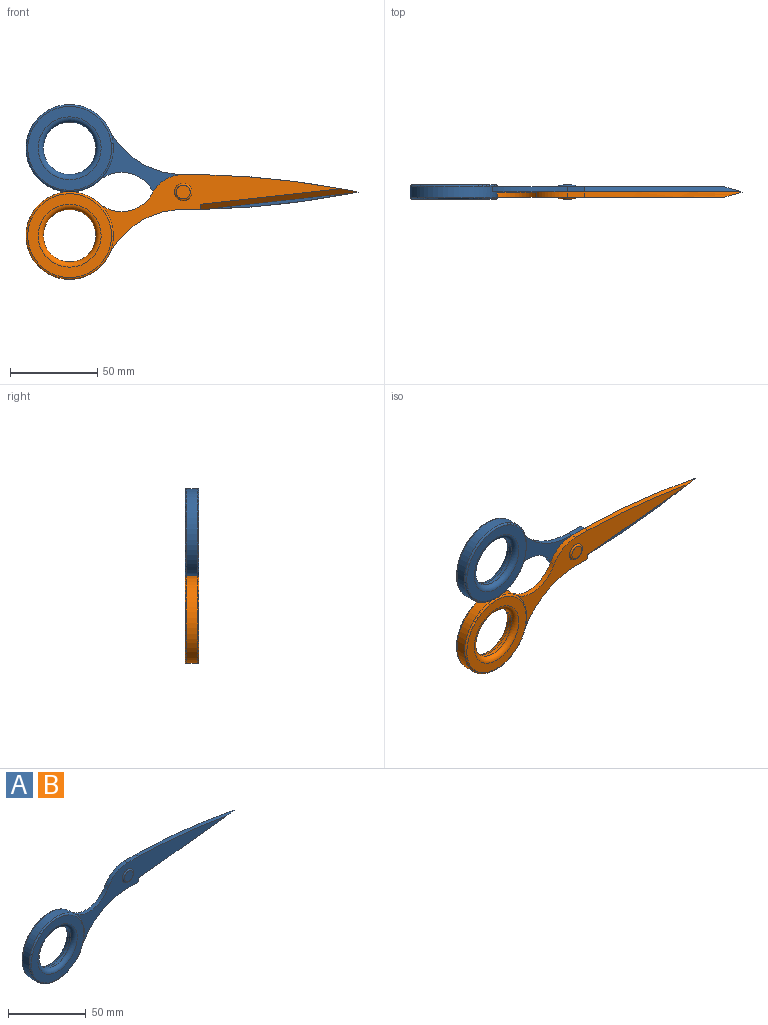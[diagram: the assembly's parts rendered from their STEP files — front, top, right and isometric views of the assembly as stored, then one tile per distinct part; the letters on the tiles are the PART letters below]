
ASSEMBLY  parts=2 mates=1
PART A: 20 faces, bbox 192.1x8x62.1 mm
  f0: plane 138.65x46.27mm, normal (0,-1,0), area 1502.5mm2, adj f2,f3,f4,f6,f7,f8,f13,f14
  f1: plane 148.49x46.27mm, normal (0,1,0), area 1836.4mm2, adj f2,f3,f4,f5,f6,f7,f8,f13
  f2: cylinder r=47.81mm len=42.68mm, axis (0,1,0), area 158.3mm2, adj f0,f1,f5,f6
  f3: cylinder r=20mm len=17.32mm, axis (0,1,0), area 62.8mm2, adj f0,f1,f4,f8
  f4: cylinder r=20mm len=31.17mm, axis (0,1,0), area 110.2mm2, adj f0,f1,f3,f5
  f5: cylinder r=25mm len=50mm, axis (0,1,0), area 843.7mm2, adj f1,f2,f4,f17,f18
  f6: plane 10x3mm, normal (0,0,-1), area 30mm2, adj f0,f1,f2,f14
  f7: cylinder r=500mm len=90mm, axis (0,1,0), area 257.2mm2, adj f0,f1,f8,f13
  f8: plane 10x3mm, normal (0,0,1), area 30mm2, adj f0,f1,f3,f7
  f9: plane 48x48mm, normal (0,1,0), area 791.7mm2, adj f16,f17
  f10: cylinder r=15mm len=30mm, axis (0,1,0), area 188.5mm2, adj f15,f16
  f11: plane 48x48mm, normal (0,-1,0), area 791.7mm2, adj f15,f18
  f12: plane 8x8mm, normal (0,-1,0), area 50.3mm2, adj f19
  f13: plane 90x11.91mm, normal (0.08,-0.7,-0.7), area 362.3mm2, adj f0,f1,f7,f14
  f14: plane 3x3mm, normal (1,0,0), area 4.5mm2, adj f0,f6,f13
  f15: torus R=18mm, axis (0,-1,0), area 476.4mm2, adj f10,f11
  f16: torus R=18mm, axis (0,-1,0), area 476.4mm2, adj f9,f10
  f17: torus R=24mm, axis (0,-1,0), area 243.2mm2, adj f5,f9
  f18: torus R=24mm, axis (0,-1,0), area 243.2mm2, adj f0,f5,f11
  f19: torus R=4mm, axis (0,-1,0), area 45.8mm2, adj f0,f12
PART B: same geometry as A
PLACE A rot(axis=(1,0,0),180deg) t=(0,0,0)mm
PLACE B at identity fixed
MATE revolute B.f19 <-> A.f19  axis (0,-1,0) through (0,0,0)mm
